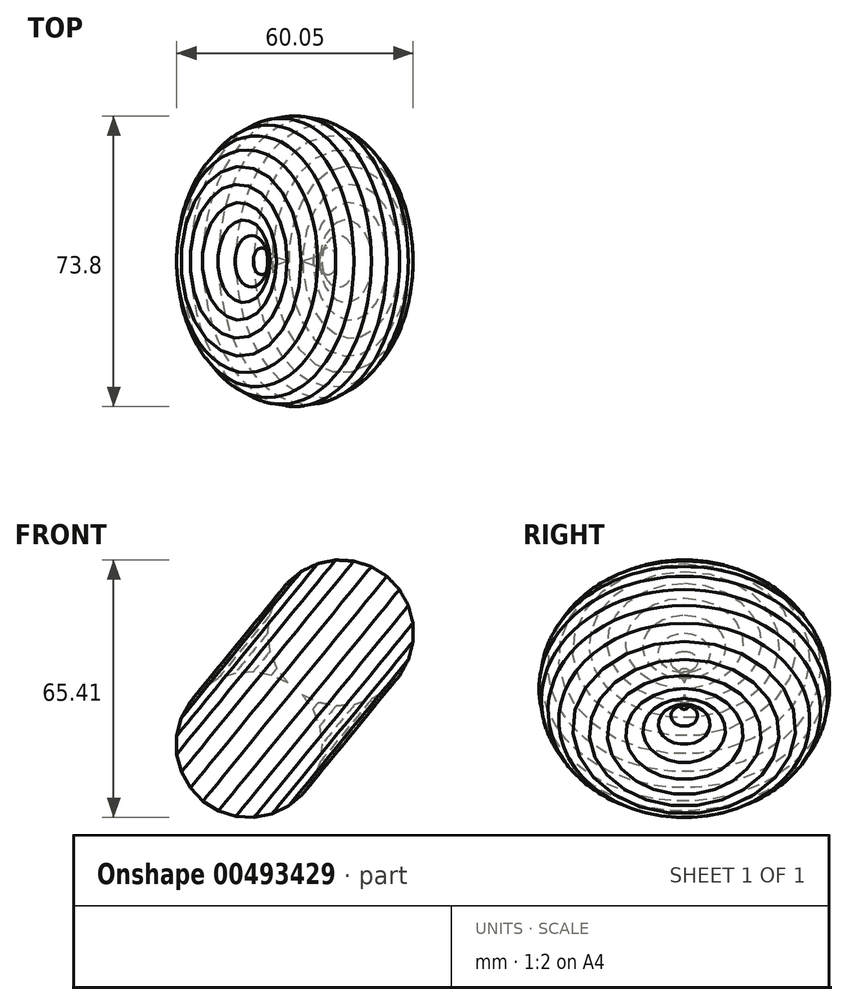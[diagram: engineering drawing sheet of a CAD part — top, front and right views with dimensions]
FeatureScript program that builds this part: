
annotation { "Feature Type Name" : "Feature", "Feature Type Description" : "" }
export const myFeature = defineFeature(function(context is Context, id is Id, definition is map)
    precondition{}
    {
        {
            var Q0;
            Q0=qCreatedBy(makeId("Front.planeOp"),FACE);
            var sketch = newSketch(context, id + "F0", { "sketchPlane" : qUnion([Q0])});
            skCircle(sketch, "E0.cCircle", {"center": v(0, 0) * mm, "radius": 18.38 * mm, "construction": true});
            skLineSegment(sketch, "E0.0", {"start": v(13.57, -12.6) * mm, "end": v(10.01, -15.58) * mm});
            skLineSegment(sketch, "E0.1", {"start": v(10.01, -15.58) * mm, "end": v(5.82, -17.58) * mm});
            skLineSegment(sketch, "E0.2", {"start": v(5.82, -17.58) * mm, "end": v(1.27, -18.48) * mm});
            skLineSegment(sketch, "E0.3", {"start": v(1.27, -18.48) * mm, "end": v(-3.37, -18.21) * mm});
            skLineSegment(sketch, "E0.4", {"start": v(-3.37, -18.21) * mm, "end": v(-7.8, -16.8) * mm});
            skLineSegment(sketch, "E0.5", {"start": v(-7.8, -16.8) * mm, "end": v(-11.73, -14.34) * mm});
            skLineSegment(sketch, "E0.6", {"start": v(-11.73, -14.34) * mm, "end": v(-14.92, -10.97) * mm});
            skLineSegment(sketch, "E0.7", {"start": v(-14.92, -10.97) * mm, "end": v(-17.18, -6.91) * mm});
            skLineSegment(sketch, "E0.8", {"start": v(-17.18, -6.91) * mm, "end": v(-18.36, -2.42) * mm});
            skLineSegment(sketch, "E0.9", {"start": v(-18.36, -2.42) * mm, "end": v(-18.39, 2.22) * mm});
            skLineSegment(sketch, "E0.10", {"start": v(-18.39, 2.22) * mm, "end": v(-17.26, 6.72) * mm});
            skLineSegment(sketch, "E0.11", {"start": v(-17.26, 6.72) * mm, "end": v(-15.05, 10.8) * mm});
            skLineSegment(sketch, "E0.12", {"start": v(-15.05, 10.8) * mm, "end": v(-11.89, 14.2) * mm});
            skLineSegment(sketch, "E0.13", {"start": v(-11.89, 14.2) * mm, "end": v(-7.98, 16.72) * mm});
            skLineSegment(sketch, "E0.14", {"start": v(-7.98, 16.72) * mm, "end": v(-3.57, 18.18) * mm});
            skLineSegment(sketch, "E0.15", {"start": v(-3.57, 18.18) * mm, "end": v(1.06, 18.5) * mm});
            skLineSegment(sketch, "E0.16", {"start": v(1.06, 18.5) * mm, "end": v(5.63, 17.65) * mm});
            skLineSegment(sketch, "E0.17", {"start": v(5.63, 17.65) * mm, "end": v(9.84, 15.7) * mm});
            skLineSegment(sketch, "E0.18", {"start": v(9.84, 15.7) * mm, "end": v(13.43, 12.75) * mm});
            skLineSegment(sketch, "E0.19", {"start": v(13.43, 12.75) * mm, "end": v(16.18, 9.01) * mm});
            skLineSegment(sketch, "E0.20", {"start": v(16.18, 9.01) * mm, "end": v(17.91, 4.7) * mm});
            skLineSegment(sketch, "E0.21", {"start": v(17.91, 4.7) * mm, "end": v(18.52, 0.1) * mm});
            skLineSegment(sketch, "E0.22", {"start": v(18.52, 0.1) * mm, "end": v(17.97, -4.5) * mm});
            skLineSegment(sketch, "E0.23", {"start": v(17.97, -4.5) * mm, "end": v(16.28, -8.83) * mm});
            skLineSegment(sketch, "E0.24", {"start": v(16.28, -8.83) * mm, "end": v(13.57, -12.6) * mm});
            skPoint(sketch, "E0.0.midPoint", {"position": v(11.8, -14.1) * mm});
            skSolve(sketch);
        }
        {
            var Q0;
            Q0=makeQuery(id+"F0.imprint","IMPRINT",FACE,{"disambiguationData":[TD([[makeQuery(id+"F0.imprint","IMPRINT",EDGE,{"derivedFrom":sQuery(id+"F0.wireOp",EDGE,"E0.0")}),-1.0]])]});
            var Q1;
            Q1=sQuery(id+"F0.wireOp",EDGE,"E0.18");
            revolve(context, id + "F1", {"entities" : qUnion([Q0]), "axis" : qUnion([Q1]), "revolveType" : RevolveType.FULL});
        }
    });
